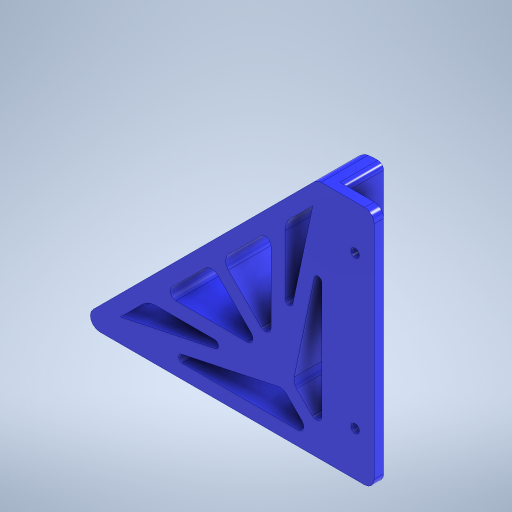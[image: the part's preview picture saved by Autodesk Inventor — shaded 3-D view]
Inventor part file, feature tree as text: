
AUTODESK INVENTOR PART (.ipt)
format: ipt  version: 2024.1 (Build 281209000, 209)  size: 580,608 bytes
history: native  units: mm
features: fillet x7, sketch x6, extrude x5, projected_geometry x3, hole x2, chamfer x1
ambient origin geometry x8: Origin, YZ Plane, XZ Plane, XY Plane, X Axis, Y Axis, Z Axis, Center Point
bodies: Body1 (feature_tree)
feature tree (24):
  extrude  "Extrusion3"  Depth=4.0mm
  fillet  "Fillet2"  Radius=175.0mm
  hole  "Hole4"  [1 undecoded]
  sketch  "Sketch7"  dims[d46=5.0mm]
  extrude  "Extrusion5"  Depth=10.0mm
  extrude  "Extrusion6"  Depth=23.285mm
  fillet  "Fillet4"  Radius=7.5mm
  fillet  "Fillet6"  Radius=20.0mm
  extrude  "Extrusion7"  Depth=10.0mm
  hole  "Hole6"  [1 undecoded]
  fillet  "Fillet9"  Radius=7.5mm
  fillet  "Fillet10"  Radius=20.0mm
  fillet  "Fillet11"  Radius=7.5mm
  extrude  "Extrusion9"  TaperAngle=0.0deg  [1 undecoded]
  chamfer  "Chamfer1"  Distance=3.0mm
  fillet  "Fillet13"  Radius=3.75mm
  sketch  "Sketch1"  dims[d3=30.0mm d41=4.0mm d42=175.0mm]
  sketch  "Sketch6"  dims[d43=45.0deg d44=5.0mm d45=0.0mm]
  sketch  "Sketch10"  dims[d47=4.5mm d48=6.0mm d49=9.4mm d50=2.0mm d51=90.0deg d52=39.95mm d53=0.0mm d54=10.0mm]
  sketch  "Sketch11"  dims[d55=80.0mm d56=23.285mm d57=7.5mm d58=20.0mm]
  sketch  "Sketch13"  dims[d61=7.5mm d63=7.5mm d66=3.75mm d67=7.5mm d68=20.0mm d69=0.0mm d70=7.5mm d71=0.0mm d72=0.0mm d74=3.0mm d75=3.75mm d77=5.0mm d91=10.0mm d93=15.0mm d95=62.25mm d96=15.24mm d97=10.0mm d98=0.0mm d101=6.2mm d102=6.0mm d103=9.4mm d104=2.0mm d105=90.0deg d106=8.0mm d107=0.0mm d108=7.62mm d111=54.952633mm d112=49.952633mm d115=3.0mm d116=8.0mm d117=2.0mm d119=10.0mm d120=0.0mm d121=2.0mm d122=2.0mm d123=45.0deg d124=10.0mm d118=0.0mm]
  projected_geometry  "Projected Loop3"
  projected_geometry  "Projected Loop4"
  projected_geometry  "Project Cut Edges1"
note: 3 required parameter values undecoded (feature->parameter linkage not recoverable at this tier; creation-order binding heuristic only, values carry confidence <= 0.55)
